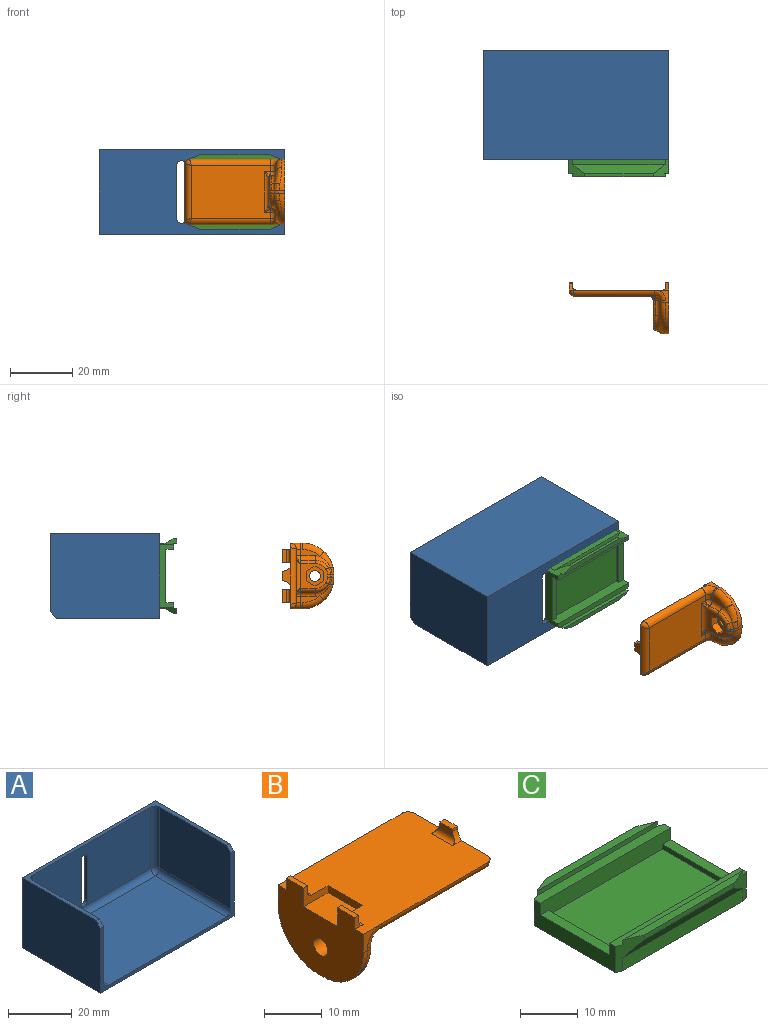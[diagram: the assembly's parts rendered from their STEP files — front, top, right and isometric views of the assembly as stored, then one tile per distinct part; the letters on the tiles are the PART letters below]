
ASSEMBLY  parts=3 mates=2
PART A: 23 faces, bbox 59.4x35x27 mm
  f0: plane 59.4x25mm, normal (0,-1,0), area 151mm2, adj f1,f3,f5,f6,f8,f9,f10,f11
  f1: plane 35x27mm, normal (1,0,0), area 943mm2, adj f0,f2,f4,f5,f11
  f2: plane 59.4x27mm, normal (0,1,0), area 1545.7mm2, adj f1,f3,f4,f5,f19,f20,f21,f22
  f3: plane 35x27mm, normal (-1,0,0), area 943mm2, adj f0,f2,f4,f5,f10
  f4: plane 59.4x33mm, normal (0,0,1), area 173.4mm2, adj f1,f2,f3,f6,f7,f8,f10,f11
  f5: plane 59.4x35mm, normal (0,0,-1), area 2079mm2, adj f0,f1,f2,f3
  f6: plane 31.6x23.6mm, normal (-1,0,0), area 743.8mm2, adj f0,f4,f11,f12,f13
  f7: plane 52.6x23.6mm, normal (0,-1,0), area 1183.3mm2, adj f4,f12,f15,f18,f19,f20,f21,f22
  f8: plane 31.6x23.6mm, normal (1,0,0), area 743.8mm2, adj f0,f4,f10,f16,f18
  f9: plane 52.6x31.6mm, normal (0,0,1), area 1662.2mm2, adj f0,f13,f15,f16
  f10: plane 2x2mm, normal (0,-0.71,0.71), area 4mm2, adj f0,f3,f4,f8
  f11: plane 2x2mm, normal (0,-0.71,0.71), area 4mm2, adj f0,f1,f4,f6
  f12: cylinder r=2mm len=23.6mm, axis (0,0,1), area 74.1mm2, adj f4,f6,f7,f14
  f13: cylinder r=2mm len=31.6mm, axis (0,-1,0), area 99.3mm2, adj f0,f6,f9,f14
  f14: sphere r=2mm, area 6.3mm2, adj f12,f13,f15
  f15: cylinder r=2mm len=52.6mm, axis (1,0,0), area 165.2mm2, adj f7,f9,f14,f17
  f16: cylinder r=2mm len=31.6mm, axis (0,1,0), area 99.3mm2, adj f0,f8,f9,f17
  f17: sphere r=2mm, area 6.3mm2, adj f15,f16,f18
  f18: cylinder r=2mm len=23.6mm, axis (0,0,-1), area 74.1mm2, adj f4,f7,f8,f17
  f19: cylinder r=1.5mm len=3mm, axis (0,1,0), area 6.6mm2, adj f2,f7,f20,f21
  f20: plane 17x1.4mm, normal (1,0,0), area 23.8mm2, adj f2,f7,f19,f22
  f21: plane 17x1.4mm, normal (-1,0,0), area 23.8mm2, adj f2,f7,f19,f22
  f22: cylinder r=1.5mm len=3mm, axis (0,1,0), area 6.6mm2, adj f2,f7,f20,f21
PART B: 82 faces, bbox 32.9x22.7x17.6 mm
  f0: plane 5.98x2.17mm, normal (1,0,0), area 8.3mm2, adj f39,f40,f41,f56,f58
  f1: cylinder r=1.75mm len=3.5mm, axis (-1,0,0), area 27.5mm2, adj f5,f32
  f2: plane 25.5x17mm, normal (0,0,-1), area 407.5mm2, adj f39,f44,f46,f48,f49,f62,f66,f70
  f3: plane 5.98x2.17mm, normal (1,0,0), area 8.3mm2, adj f48,f50,f52,f65,f67
  f4: plane 32.05x21.05mm, normal (0,0,1), area 592.5mm2, adj f5,f8,f9,f10,f11,f12,f14,f16
  f5: plane 21x16.5mm, normal (-1,0,0), area 249.9mm2, adj f1,f4,f8,f9,f12,f14,f16,f17
  f6: plane 5.16x2.5mm, normal (1,0,0), area 9.4mm2, adj f10,f11,f22,f23,f24,f66
  f7: plane 3.79x1.5mm, normal (-1,0,0), area 5mm2, adj f10,f11,f22,f23,f24,f27
  f8: plane 4.5x4mm, normal (0,-1,0), area 6.6mm2, adj f4,f5,f29,f67,f69
  f9: plane 4.5x4mm, normal (0,1,0), area 6.6mm2, adj f4,f5,f30,f58,f60
  f10: cylinder r=3.99mm len=2.2mm, axis (1,0,0), area 3.3mm2, adj f4,f6,f7,f23,f27
  f11: cylinder r=3.99mm len=2.2mm, axis (1,0,0), area 3.3mm2, adj f4,f6,f7,f22,f27
  f12: plane 6x4mm, normal (0,-1,0), area 11.7mm2, adj f4,f5,f13,f18,f19,f20,f26
  f13: plane 4.2x1.5mm, normal (1,0,0), area 6.3mm2, adj f12,f14,f20,f26
  f14: plane 2.5x2mm, normal (0,1,0), area 2.7mm2, adj f4,f5,f13,f20,f26
  f15: plane 4.2x1.5mm, normal (1,0,0), area 6.3mm2, adj f16,f17,f21,f25
  f16: plane 6x4mm, normal (0,1,0), area 11.7mm2, adj f4,f5,f15,f18,f19,f21,f25
  f17: plane 2.5x2mm, normal (0,-1,0), area 2.7mm2, adj f4,f5,f15,f21,f25
  f18: plane 8.4x1.5mm, normal (-1,0,0), area 12.6mm2, adj f4,f12,f16,f19
  f19: plane 8.4x6mm, normal (0,0,1), area 50.4mm2, adj f5,f12,f16,f18
  f20: plane 4.2x1mm, normal (0,0,1), area 4.2mm2, adj f5,f12,f13,f14
  f21: plane 4.2x1mm, normal (0,0,1), area 4.2mm2, adj f5,f15,f16,f17
  f22: plane 1.2x0.5mm, normal (0,-1,0), area 0.6mm2, adj f6,f7,f11,f24
  f23: plane 1.2x0.5mm, normal (0,1,0), area 0.6mm2, adj f6,f7,f10,f24
  f24: plane 3.14x1.2mm, normal (0,0,1), area 3.8mm2, adj f6,f7,f22,f23
  f25: cylinder r=1mm len=4.2mm, axis (0,1,0), area 6.6mm2, adj f4,f15,f16,f17
  f26: cylinder r=1mm len=4.2mm, axis (0,1,0), area 6.6mm2, adj f4,f12,f13,f14
  f27: cylinder r=1mm len=5.16mm, axis (0,-1,0), area 7mm2, adj f4,f7,f10,f11
  f28: plane 1.96x1mm, normal (0,0,-1), area 2mm2, adj f5,f29,f30,f55,f57,f59
  f29: cylinder r=10mm len=10mm, axis (-1,0,0), area 19.5mm2, adj f5,f8,f28,f61,f63,f65
  f30: cylinder r=10mm len=10mm, axis (1,0,0), area 19.5mm2, adj f5,f9,f28,f53,f54,f56
  f31: plane 8.54x8.1mm, normal (1,0,0), area 36mm2, adj f33,f34,f35,f36,f37,f38,f46,f73
  f32: plane 6.35x5.5mm, normal (1,0,0), area 16.6mm2, adj f1,f33,f34,f35,f36,f37,f38
  f33: plane 2.75x2.5mm, normal (0,0.87,0.5), area 7.9mm2, adj f31,f32,f34,f38
  f34: plane 3.18x2.5mm, normal (0,0,1), area 7.9mm2, adj f31,f32,f33,f35
  f35: plane 2.75x2.5mm, normal (0,-0.87,0.5), area 7.9mm2, adj f31,f32,f34,f36
  f36: plane 2.75x2.5mm, normal (0,-0.87,-0.5), area 7.9mm2, adj f31,f32,f35,f37
  f37: plane 3.18x2.5mm, normal (0,0,-1), area 7.9mm2, adj f31,f32,f36,f38
  f38: plane 2.75x2.5mm, normal (0,0.87,-0.5), area 7.9mm2, adj f31,f32,f33,f37
  f39: cylinder r=1.5mm len=2mm, axis (0,1,0), area 4.7mm2, adj f0,f2,f42,f60
  f40: cylinder r=1.5mm len=4.5mm, axis (0,0,1), area 9.2mm2, adj f0,f41,f42,f73
  f41: torus R=6.5mm, axis (1,0,0), area 9.6mm2, adj f0,f40,f43,f54,f74
  f42: sphere r=1.5mm, area 3.4mm2, adj f39,f40,f44,f72
  f43: bspline ~4.12x1.98mm, area 2.3mm2, adj f41,f45,f53,f55,f75
  f44: cylinder r=1.5mm len=2mm, axis (1,0,0), area 1.4mm2, adj f2,f42,f71
  f45: bspline ~1.77x1.44mm, area 0.8mm2, adj f43,f47,f57,f76
  f46: cylinder r=1.5mm len=13mm, axis (0,1,0), area 23.6mm2, adj f2,f31,f71,f72,f80,f81
  f47: bspline ~4.6x2.02mm, area 2.3mm2, adj f45,f50,f59,f61,f77
  f48: cylinder r=1.5mm len=2mm, axis (0,1,0), area 4.7mm2, adj f2,f3,f51,f69
  f49: cylinder r=1.5mm len=2mm, axis (-1,0,0), area 1.4mm2, adj f2,f51,f80
  f50: torus R=6.5mm, axis (1,0,0), area 9.6mm2, adj f3,f47,f52,f63,f78
  f51: sphere r=1.5mm, area 3.4mm2, adj f48,f49,f52,f81
  f52: cylinder r=1.5mm len=4.5mm, axis (0,0,-1), area 9.2mm2, adj f3,f50,f51,f79
  f53: bspline ~3.34x1.73mm, area 4mm2, adj f30,f43,f54,f55
  f54: bspline ~8.32x5.78mm, area 13.8mm2, adj f30,f41,f53,f56
  f55: bspline ~1.95x1.64mm, area 0.2mm2, adj f28,f43,f53,f57
  f56: torus R=8mm, axis (1,0,0), area 22mm2, adj f0,f30,f54,f58
  f57: bspline ~1.43x1.32mm, area 1.3mm2, adj f28,f45,f55,f59
  f58: cylinder r=2mm len=2mm, axis (0,0,-1), area 1.6mm2, adj f0,f9,f56,f60
  f59: bspline ~2.05x1.55mm, area 0.2mm2, adj f28,f47,f57,f61
  f60: torus R=3.5mm, axis (0,-1,0), area 11mm2, adj f9,f39,f58,f62
  f61: bspline ~3.43x1.75mm, area 4mm2, adj f29,f47,f59,f63
  f62: cylinder r=2mm len=26mm, axis (-1,0,0), area 80.9mm2, adj f2,f4,f60,f64
  f63: bspline ~6.66x5.6mm, area 13.8mm2, adj f29,f50,f61,f65
  f64: bspline ~2.11x2mm, area 3.3mm2, adj f4,f62,f66
  f65: torus R=8mm, axis (1,0,0), area 22mm2, adj f3,f29,f63,f67
  f66: cylinder r=2mm len=18mm, axis (0,1,0), area 55mm2, adj f2,f4,f6,f64,f68
  f67: cylinder r=2mm len=2mm, axis (0,0,1), area 1.6mm2, adj f3,f8,f65,f69
  f68: bspline ~2.11x2mm, area 3.3mm2, adj f4,f66,f70
  f69: torus R=3.5mm, axis (0,-1,0), area 11mm2, adj f8,f48,f67,f70
  f70: cylinder r=2mm len=26mm, axis (1,0,0), area 80.9mm2, adj f2,f4,f68,f69
  f71: bspline ~2.12x2.12mm, area 0.9mm2, adj f44,f46,f72
  f72: bspline ~1.45x1.28mm, area 1.2mm2, adj f42,f46,f71,f73
  f73: cylinder r=1mm len=4.5mm, axis (0,0,1), area 6.2mm2, adj f31,f40,f72,f74
  f74: torus R=4.05mm, axis (-1,0,0), area 6.6mm2, adj f31,f41,f73,f75
  f75: bspline ~2.59x1.6mm, area 2.9mm2, adj f31,f43,f74,f76
  f76: bspline ~1.01x1mm, area 1mm2, adj f31,f45,f75,f77
  f77: bspline ~3x1.77mm, area 2.9mm2, adj f31,f47,f76,f78
  f78: torus R=4.05mm, axis (-1,0,0), area 6.6mm2, adj f31,f50,f77,f79
  f79: cylinder r=1mm len=4.5mm, axis (0,0,-1), area 6.2mm2, adj f31,f52,f78,f81
  f80: bspline ~2.12x2.12mm, area 0.9mm2, adj f46,f49,f81
  f81: bspline ~1.45x1.28mm, area 1.2mm2, adj f46,f51,f79,f80
PART C: 26 faces, bbox 32x24x6.5 mm
  f0: plane 32x2mm, normal (0,0,1), area 63.4mm2, adj f1,f3,f10,f14,f22,f25
  f1: plane 20x5.5mm, normal (1,0,0), area 67.5mm2, adj f0,f5,f6,f8,f10,f13,f22,f24
  f2: plane 29.5x2.75mm, normal (0,1,0), area 81.1mm2, adj f6,f19,f23,f24
  f3: plane 20x5.5mm, normal (-1,0,0), area 67.5mm2, adj f0,f5,f6,f8,f10,f12,f23,f25
  f4: plane 29.5x2.75mm, normal (0,-1,0), area 81.1mm2, adj f6,f16,f22,f25
  f5: plane 32x2mm, normal (0,0,1), area 63.4mm2, adj f1,f3,f8,f18,f23,f24
  f6: plane 32x21mm, normal (0,0,-1), area 670.7mm2, adj f1,f2,f3,f4,f22,f23,f24,f25
  f7: plane 17x1mm, normal (-1,0,0), area 17mm2, adj f8,f10,f11,f13
  f8: plane 32x3.5mm, normal (0,-1,0), area 108mm2, adj f1,f3,f5,f7,f9,f11,f12,f13
  f9: plane 17x1mm, normal (1,0,0), area 17mm2, adj f8,f10,f11,f12
  f10: plane 32x3.5mm, normal (0,1,0), area 108mm2, adj f0,f1,f3,f7,f9,f11,f12,f13
  f11: plane 28x17mm, normal (0,0,1), area 476mm2, adj f7,f8,f9,f10
  f12: plane 17x2mm, normal (0,0,1), area 34mm2, adj f3,f8,f9,f10
  f13: plane 17x2mm, normal (0,0,1), area 34mm2, adj f1,f7,f8,f10
  f14: plane 29.5x1mm, normal (0,1,0), area 29.5mm2, adj f0,f17,f22,f25
  f15: plane 22x1mm, normal (0,-1,0), area 22mm2, adj f16,f17,f22,f25
  f16: plane 29.5x2.75mm, normal (0,-0.88,-0.48), area 80.7mm2, adj f4,f15,f22,f25
  f17: plane 29.5x1.5mm, normal (0,0,1), area 38.6mm2, adj f14,f15,f22,f25
  f18: plane 29.5x1mm, normal (0,-1,0), area 29.5mm2, adj f5,f21,f23,f24
  f19: plane 29.5x2.75mm, normal (0,0.88,-0.48), area 80.7mm2, adj f2,f20,f23,f24
  f20: plane 22x1mm, normal (0,1,0), area 22mm2, adj f19,f21,f23,f24
  f21: plane 29.5x1.5mm, normal (0,0,1), area 38.6mm2, adj f18,f20,f23,f24
  f22: plane 6.5x5mm, normal (0.37,-0.93,0), area 17mm2, adj f0,f1,f4,f6,f14,f15,f16,f17
  f23: plane 6.5x5mm, normal (-0.37,0.93,0), area 17mm2, adj f2,f3,f5,f6,f18,f19,f20,f21
  f24: plane 6.5x5mm, normal (0.37,0.93,0), area 17mm2, adj f1,f2,f5,f6,f18,f19,f20,f21
  f25: plane 6.5x5mm, normal (-0.37,-0.93,0), area 17mm2, adj f0,f3,f4,f6,f14,f15,f16,f17
PLACE A rot(axis=(-1,0,0),180deg) t=(23.45,21.98,1.17)mm fixed
PLACE B rot(axis=(0,0.71,0.71),180deg) t=(37.29,-39.3,-12.33)mm
PLACE C rot(axis=(1,0,0),90deg) t=(33.67,5.48,-11.73)mm
MATE parallel C.f11 <-> B.f4  axis (0,-1,0) through (37.27,3.48,-12.33)mm
MATE parallel A.f2 <-> C.f6  axis (0,-1,0) through (23.57,4.48,-12.33)mm
